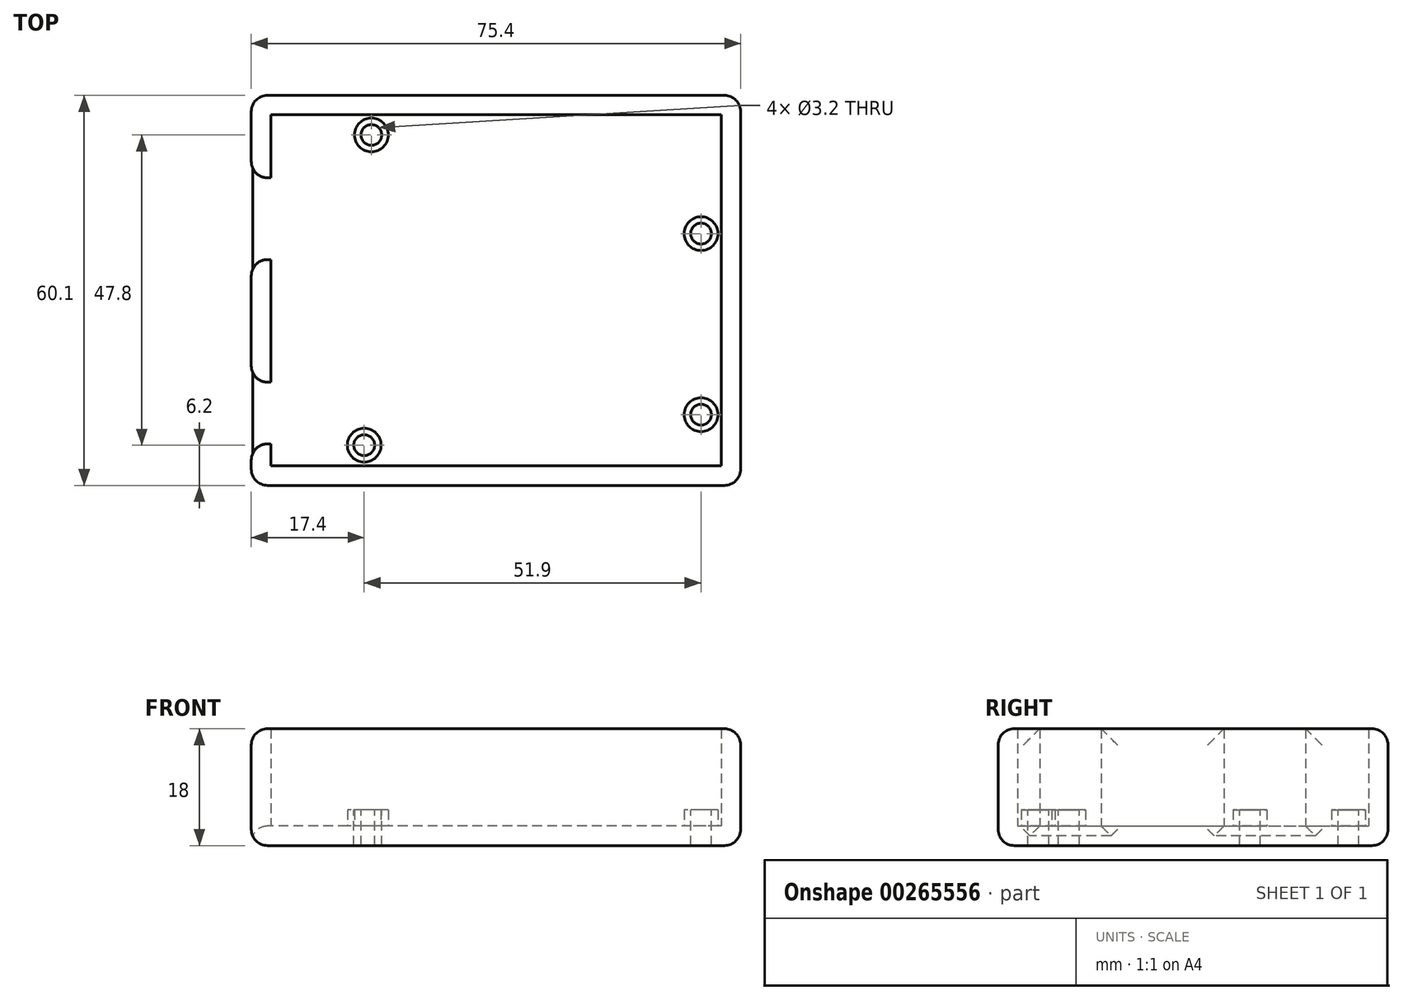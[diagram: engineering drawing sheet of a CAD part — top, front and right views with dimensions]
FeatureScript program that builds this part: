
annotation { "Feature Type Name" : "Feature", "Feature Type Description" : "" }
export const myFeature = defineFeature(function(context is Context, id is Id, definition is map)
    precondition{}
    {
        {
            var Q0;
            Q0=qCreatedBy(makeId("Top.planeOp"),FACE);
            var sketch = newSketch(context, id + "F0", { "sketchPlane" : qUnion([Q0])});
            skLineSegment(sketch, "E0.bottom", {"start": v(34.3, -26.65) * mm, "end": v(-34.3, -26.65) * mm});
            skLineSegment(sketch, "E0.top", {"start": v(34.3, 26.65) * mm, "end": v(-34.3, 26.65) * mm});
            skLineSegment(sketch, "E0.left", {"start": v(34.3, -26.65) * mm, "end": v(34.3, 26.65) * mm});
            skLineSegment(sketch, "E0.right", {"start": v(-34.3, -26.65) * mm, "end": v(-34.3, 26.65) * mm});
            skPoint(sketch, "E0.middle", {"position": v(0, 0) * mm});
            skCircle(sketch, "E1", {"center": v(-19.2, 23.95) * mm, "radius": 1.6 * mm});
            skCircle(sketch, "E2", {"center": v(31.6, 8.75) * mm, "radius": 1.6 * mm});
            skCircle(sketch, "E3", {"center": v(31.6, -19.15) * mm, "radius": 1.6 * mm});
            skCircle(sketch, "E4", {"center": v(-20.3, -23.85) * mm, "radius": 1.6 * mm});
            skLineSegment(sketch, "E5.0", {"start": v(34.7, 27.05) * mm, "end": v(-34.7, 27.05) * mm});
            skLineSegment(sketch, "E5.1", {"start": v(34.7, -27.05) * mm, "end": v(34.7, 27.05) * mm});
            skLineSegment(sketch, "E5.2", {"start": v(34.7, -27.05) * mm, "end": v(-34.7, -27.05) * mm});
            skLineSegment(sketch, "E5.3", {"start": v(-34.7, -27.05) * mm, "end": v(-34.7, 27.05) * mm});
            skLineSegment(sketch, "E6.0", {"start": v(37.7, 30.05) * mm, "end": v(-37.7, 30.05) * mm});
            skLineSegment(sketch, "E6.1", {"start": v(37.7, -30.05) * mm, "end": v(37.7, 30.05) * mm});
            skLineSegment(sketch, "E6.2", {"start": v(37.7, -30.05) * mm, "end": v(-37.7, -30.05) * mm});
            skLineSegment(sketch, "E6.3", {"start": v(-37.7, -30.05) * mm, "end": v(-37.7, 30.05) * mm});
            skLineSegment(sketch, "E7.bottom", {"start": v(-24, 5.05) * mm, "end": v(-40.5, 5.05) * mm});
            skLineSegment(sketch, "E7.top", {"start": v(-24, 17.05) * mm, "end": v(-40.5, 17.05) * mm});
            skLineSegment(sketch, "E7.left", {"start": v(-24, 5.05) * mm, "end": v(-24, 17.05) * mm});
            skLineSegment(sketch, "E7.right", {"start": v(-40.5, 5.05) * mm, "end": v(-40.5, 17.05) * mm});
            skPoint(sketch, "E7.middle", {"position": v(-32.25, 11.05) * mm});
            skLineSegment(sketch, "E8.bottom", {"start": v(-24.8, -23.35) * mm, "end": v(-39.3, -23.35) * mm});
            skLineSegment(sketch, "E8.top", {"start": v(-24.8, -14.45) * mm, "end": v(-39.3, -14.45) * mm});
            skLineSegment(sketch, "E8.left", {"start": v(-24.8, -23.35) * mm, "end": v(-24.8, -14.45) * mm});
            skLineSegment(sketch, "E8.right", {"start": v(-39.3, -23.35) * mm, "end": v(-39.3, -14.45) * mm});
            skPoint(sketch, "E8.middle", {"position": v(-32.05, -18.9) * mm});
            skCircle(sketch, "E9.0", {"center": v(-19.2, 23.95) * mm, "radius": 2.6 * mm});
            skCircle(sketch, "E10.0", {"center": v(-20.3, -23.85) * mm, "radius": 2.6 * mm});
            skCircle(sketch, "E11.0", {"center": v(31.6, -19.15) * mm, "radius": 2.6 * mm});
            skCircle(sketch, "E12.0", {"center": v(31.6, 8.75) * mm, "radius": 2.6 * mm});
            skLineSegment(sketch, "E13.0", {"start": v(-23.7, 4.75) * mm, "end": v(-40.8, 4.75) * mm});
            skLineSegment(sketch, "E13.1", {"start": v(-23.7, 4.75) * mm, "end": v(-23.7, 17.35) * mm});
            skLineSegment(sketch, "E13.2", {"start": v(-23.7, 17.35) * mm, "end": v(-40.8, 17.35) * mm});
            skLineSegment(sketch, "E13.3", {"start": v(-40.8, 4.75) * mm, "end": v(-40.8, 17.35) * mm});
            skLineSegment(sketch, "E14.0", {"start": v(-24.5, -14.15) * mm, "end": v(-39.6, -14.15) * mm});
            skLineSegment(sketch, "E14.1", {"start": v(-24.5, -23.65) * mm, "end": v(-24.5, -14.15) * mm});
            skLineSegment(sketch, "E14.2", {"start": v(-24.5, -23.65) * mm, "end": v(-39.6, -23.65) * mm});
            skLineSegment(sketch, "E14.3", {"start": v(-39.6, -23.65) * mm, "end": v(-39.6, -14.15) * mm});
            skSolve(sketch);
        }
        {
            var Q0;
            {var subQ4=sQuery(id+"F0.wireOp",EDGE,"E5.0");Q0=makeQuery(id+"F0.imprint","IMPRINT",FACE,{"disambiguationData":[TD([[makeQuery(id+"F0.imprint","IMPRINT",EDGE,{"derivedFrom":subQ4}),-1.0]])]});}
            var Q1;
            {var subQ0=sQuery(id+"F0.wireOp",EDGE,"E8.top");var subQ1=sQuery(id+"F0.wireOp",EDGE,"E0.right");var subQ2=makeQuery(id+"F0.imprint","INTERSECT",VERTEX,{"derivedFrom":[subQ1,subQ0]});Q1=makeQuery(id+"F0.imprint","IMPRINT",FACE,{"disambiguationData":[TD([[makeQuery(id+"F0.imprint","IMPRINT",EDGE,{"disambiguationData":[TD([[subQ2,-1.0]])],"derivedFrom":subQ1}),1.0]])]});}
            var Q2;
            {var subQ0=sQuery(id+"F0.wireOp",EDGE,"E8.bottom");var subQ1=sQuery(id+"F0.wireOp",EDGE,"E0.right");var subQ2=makeQuery(id+"F0.imprint","INTERSECT",VERTEX,{"derivedFrom":[subQ1,subQ0]});Q2=makeQuery(id+"F0.imprint","IMPRINT",FACE,{"disambiguationData":[TD([[makeQuery(id+"F0.imprint","IMPRINT",EDGE,{"disambiguationData":[TD([[subQ2,-1.0]])],"derivedFrom":subQ1}),1.0]])]});}
            var Q3;
            {var subQ0=sQuery(id+"F0.wireOp",EDGE,"E8.bottom");var subQ1=sQuery(id+"F0.wireOp",EDGE,"E0.right");var subQ2=makeQuery(id+"F0.imprint","INTERSECT",VERTEX,{"derivedFrom":[subQ1,subQ0]});Q3=makeQuery(id+"F0.imprint","IMPRINT",FACE,{"disambiguationData":[TD([[makeQuery(id+"F0.imprint","IMPRINT",EDGE,{"disambiguationData":[TD([[subQ2,-1.0]])],"derivedFrom":subQ1}),-1.0]])]});}
            var Q4;
            {var subQ4=sQuery(id+"F0.wireOp",EDGE,"E0.bottom");Q4=makeQuery(id+"F0.imprint","IMPRINT",FACE,{"disambiguationData":[TD([[makeQuery(id+"F0.imprint","IMPRINT",EDGE,{"derivedFrom":subQ4}),-1.0]])]});}
            var Q5;
            {var subQ10=sQuery(id+"F0.wireOp",EDGE,"E0.bottom");Q5=makeQuery(id+"F0.imprint","IMPRINT",FACE,{"disambiguationData":[TD([[makeQuery(id+"F0.imprint","IMPRINT",EDGE,{"derivedFrom":subQ10}),1.0]])]});}
            var Q6;
            {var subQ5=sQuery(id+"F0.wireOp",EDGE,"E7.left");Q6=makeQuery(id+"F0.imprint","IMPRINT",FACE,{"disambiguationData":[TD([[makeQuery(id+"F0.imprint","IMPRINT",EDGE,{"derivedFrom":subQ5}),1.0]])]});}
            var Q7;
            {var subQ0=sQuery(id+"F0.wireOp",EDGE,"E7.bottom");var subQ1=sQuery(id+"F0.wireOp",EDGE,"E5.3");var subQ2=makeQuery(id+"F0.imprint","INTERSECT",VERTEX,{"derivedFrom":[subQ1,subQ0]});Q7=makeQuery(id+"F0.imprint","IMPRINT",FACE,{"disambiguationData":[TD([[makeQuery(id+"F0.imprint","IMPRINT",EDGE,{"disambiguationData":[TD([[subQ2,-1.0]])],"derivedFrom":subQ1}),1.0]])]});}
            var Q8;
            {var subQ0=sQuery(id+"F0.wireOp",EDGE,"E7.bottom");var subQ1=sQuery(id+"F0.wireOp",EDGE,"E0.right");var subQ2=makeQuery(id+"F0.imprint","INTERSECT",VERTEX,{"derivedFrom":[subQ1,subQ0]});Q8=makeQuery(id+"F0.imprint","IMPRINT",FACE,{"disambiguationData":[TD([[makeQuery(id+"F0.imprint","IMPRINT",EDGE,{"disambiguationData":[TD([[subQ2,-1.0]])],"derivedFrom":subQ1}),1.0]])]});}
            var Q9;
            {var subQ0=sQuery(id+"F0.wireOp",EDGE,"E8.bottom");var subQ1=sQuery(id+"F0.wireOp",EDGE,"E5.3");var subQ2=makeQuery(id+"F0.imprint","INTERSECT",VERTEX,{"derivedFrom":[subQ1,subQ0]});Q9=makeQuery(id+"F0.imprint","IMPRINT",FACE,{"disambiguationData":[TD([[makeQuery(id+"F0.imprint","IMPRINT",EDGE,{"disambiguationData":[TD([[subQ2,-1.0]])],"derivedFrom":subQ1}),1.0]])]});}
            var Q10;
            {var subQ0=sQuery(id+"F0.wireOp",EDGE,"E8.top");var subQ1=sQuery(id+"F0.wireOp",EDGE,"E5.3");var subQ2=makeQuery(id+"F0.imprint","INTERSECT",VERTEX,{"derivedFrom":[subQ1,subQ0]});Q10=makeQuery(id+"F0.imprint","IMPRINT",FACE,{"disambiguationData":[TD([[makeQuery(id+"F0.imprint","IMPRINT",EDGE,{"disambiguationData":[TD([[subQ2,-1.0]])],"derivedFrom":subQ1}),1.0]])]});}
            var Q11;
            Q11=makeQuery(id+"F0.imprint","IMPRINT",FACE,{"disambiguationData":[TD([[makeQuery(id+"F0.imprint","IMPRINT",EDGE,{"derivedFrom":sQuery(id+"F0.wireOp",EDGE,"E1")}),-1.0]])]});
            var Q12;
            Q12=makeQuery(id+"F0.imprint","IMPRINT",FACE,{"disambiguationData":[TD([[makeQuery(id+"F0.imprint","IMPRINT",EDGE,{"derivedFrom":sQuery(id+"F0.wireOp",EDGE,"E4")}),-1.0]])]});
            var Q13;
            Q13=makeQuery(id+"F0.imprint","IMPRINT",FACE,{"disambiguationData":[TD([[makeQuery(id+"F0.imprint","IMPRINT",EDGE,{"derivedFrom":sQuery(id+"F0.wireOp",EDGE,"E3")}),-1.0]])]});
            var Q14;
            Q14=makeQuery(id+"F0.imprint","IMPRINT",FACE,{"disambiguationData":[TD([[makeQuery(id+"F0.imprint","IMPRINT",EDGE,{"derivedFrom":sQuery(id+"F0.wireOp",EDGE,"E2")}),-1.0]])]});
            var Q15;
            {var subQ0=sQuery(id+"F0.wireOp",EDGE,"E13.0");var subQ1=sQuery(id+"F0.wireOp",EDGE,"E5.3");var subQ2=makeQuery(id+"F0.imprint","INTERSECT",VERTEX,{"derivedFrom":[subQ1,subQ0]});Q15=makeQuery(id+"F0.imprint","IMPRINT",FACE,{"disambiguationData":[TD([[makeQuery(id+"F0.imprint","IMPRINT",EDGE,{"disambiguationData":[TD([[subQ2,-1.0]])],"derivedFrom":subQ1}),1.0]])]});}
            var Q16;
            {var subQ0=sQuery(id+"F0.wireOp",EDGE,"E13.0");var subQ1=sQuery(id+"F0.wireOp",EDGE,"E0.right");var subQ2=makeQuery(id+"F0.imprint","INTERSECT",VERTEX,{"derivedFrom":[subQ1,subQ0]});Q16=makeQuery(id+"F0.imprint","IMPRINT",FACE,{"disambiguationData":[TD([[makeQuery(id+"F0.imprint","IMPRINT",EDGE,{"disambiguationData":[TD([[subQ2,-1.0]])],"derivedFrom":subQ1}),1.0]])]});}
            var Q17;
            {var subQ0=sQuery(id+"F0.wireOp",EDGE,"E7.left");Q17=makeQuery(id+"F0.imprint","IMPRINT",FACE,{"disambiguationData":[TD([[makeQuery(id+"F0.imprint","IMPRINT",EDGE,{"derivedFrom":subQ0}),-1.0]])]});}
            var Q18;
            {var subQ0=sQuery(id+"F0.wireOp",EDGE,"E14.0");var subQ1=sQuery(id+"F0.wireOp",EDGE,"E0.right");var subQ2=makeQuery(id+"F0.imprint","INTERSECT",VERTEX,{"derivedFrom":[subQ1,subQ0]});Q18=makeQuery(id+"F0.imprint","IMPRINT",FACE,{"disambiguationData":[TD([[makeQuery(id+"F0.imprint","IMPRINT",EDGE,{"disambiguationData":[TD([[subQ2,-1.0]])],"derivedFrom":subQ1}),1.0]])]});}
            var Q19;
            {var subQ0=sQuery(id+"F0.wireOp",EDGE,"E14.0");var subQ1=sQuery(id+"F0.wireOp",EDGE,"E5.3");var subQ2=makeQuery(id+"F0.imprint","INTERSECT",VERTEX,{"derivedFrom":[subQ1,subQ0]});Q19=makeQuery(id+"F0.imprint","IMPRINT",FACE,{"disambiguationData":[TD([[makeQuery(id+"F0.imprint","IMPRINT",EDGE,{"disambiguationData":[TD([[subQ2,-1.0]])],"derivedFrom":subQ1}),1.0]])]});}
            var Q20;
            {var subQ0=sQuery(id+"F0.wireOp",EDGE,"E8.left");Q20=makeQuery(id+"F0.imprint","IMPRINT",FACE,{"disambiguationData":[TD([[makeQuery(id+"F0.imprint","IMPRINT",EDGE,{"derivedFrom":subQ0}),-1.0]])]});}
            var Q21;
            {var subQ0=sQuery(id+"F0.wireOp",EDGE,"E7.top");var subQ1=sQuery(id+"F0.wireOp",EDGE,"E5.3");var subQ2=makeQuery(id+"F0.imprint","INTERSECT",VERTEX,{"derivedFrom":[subQ1,subQ0]});Q21=makeQuery(id+"F0.imprint","IMPRINT",FACE,{"disambiguationData":[TD([[makeQuery(id+"F0.imprint","IMPRINT",EDGE,{"disambiguationData":[TD([[subQ2,-1.0]])],"derivedFrom":subQ1}),1.0]])]});}
            var Q22;
            {var subQ0=sQuery(id+"F0.wireOp",EDGE,"E7.top");var subQ1=sQuery(id+"F0.wireOp",EDGE,"E0.right");var subQ2=makeQuery(id+"F0.imprint","INTERSECT",VERTEX,{"derivedFrom":[subQ1,subQ0]});Q22=makeQuery(id+"F0.imprint","IMPRINT",FACE,{"disambiguationData":[TD([[makeQuery(id+"F0.imprint","IMPRINT",EDGE,{"disambiguationData":[TD([[subQ2,-1.0]])],"derivedFrom":subQ1}),1.0]])]});}
            var Q23;
            {var subQ0=sQuery(id+"F0.wireOp",EDGE,"E14.2");var subQ1=sQuery(id+"F0.wireOp",EDGE,"E0.right");var subQ2=makeQuery(id+"F0.imprint","INTERSECT",VERTEX,{"derivedFrom":[subQ1,subQ0]});Q23=makeQuery(id+"F0.imprint","IMPRINT",FACE,{"disambiguationData":[TD([[makeQuery(id+"F0.imprint","IMPRINT",EDGE,{"disambiguationData":[TD([[subQ2,-1.0]])],"derivedFrom":subQ1}),1.0]])]});}
            var Q24;
            {var subQ0=sQuery(id+"F0.wireOp",EDGE,"E14.2");var subQ1=sQuery(id+"F0.wireOp",EDGE,"E5.3");var subQ2=makeQuery(id+"F0.imprint","INTERSECT",VERTEX,{"derivedFrom":[subQ1,subQ0]});Q24=makeQuery(id+"F0.imprint","IMPRINT",FACE,{"disambiguationData":[TD([[makeQuery(id+"F0.imprint","IMPRINT",EDGE,{"disambiguationData":[TD([[subQ2,-1.0]])],"derivedFrom":subQ1}),1.0]])]});}
            extrude(context, id + "F1", {"entities" : qUnion([Q0, Q1, Q2, Q3, Q4, Q5, Q6, Q7, Q8, Q9, Q10, Q11, Q12, Q13, Q14, Q15, Q16, Q17, Q18, Q19, Q20, Q21, Q22, Q23, Q24]), "oppositeDirection" : true, "depth" : 3 * mm});
        }
        {
            var Q0;
            {var subQ11=sQuery(id+"F0.wireOp",EDGE,"E5.0");Q0=makeQuery(id+"F0.imprint","IMPRINT",FACE,{"disambiguationData":[TD([[makeQuery(id+"F0.imprint","IMPRINT",EDGE,{"derivedFrom":subQ11}),-1.0]])]});}
            var Q1;
            {var subQ0=sQuery(id+"F0.wireOp",EDGE,"E14.0");var subQ1=sQuery(id+"F0.wireOp",EDGE,"E5.3");var subQ2=makeQuery(id+"F0.imprint","INTERSECT",VERTEX,{"derivedFrom":[subQ1,subQ0]});Q1=makeQuery(id+"F0.imprint","IMPRINT",FACE,{"disambiguationData":[TD([[makeQuery(id+"F0.imprint","IMPRINT",EDGE,{"disambiguationData":[TD([[subQ2,-1.0]])],"derivedFrom":subQ1}),1.0]])]});}
            extrude(context, id + "F2", {"entities" : qUnion([Q0, Q1]), "operationType" : NewBodyOperationType.ADD, "depth" : 15 * mm});
        }
        {
            var Q0;
            Q0=makeQuery(id+"F0.imprint","IMPRINT",FACE,{"disambiguationData":[TD([[makeQuery(id+"F0.imprint","IMPRINT",EDGE,{"derivedFrom":sQuery(id+"F0.wireOp",EDGE,"E4")}),-1.0]])]});
            var Q1;
            Q1=makeQuery(id+"F0.imprint","IMPRINT",FACE,{"disambiguationData":[TD([[makeQuery(id+"F0.imprint","IMPRINT",EDGE,{"derivedFrom":sQuery(id+"F0.wireOp",EDGE,"E1")}),-1.0]])]});
            var Q2;
            Q2=makeQuery(id+"F0.imprint","IMPRINT",FACE,{"disambiguationData":[TD([[makeQuery(id+"F0.imprint","IMPRINT",EDGE,{"derivedFrom":sQuery(id+"F0.wireOp",EDGE,"E2")}),-1.0]])]});
            var Q3;
            Q3=makeQuery(id+"F0.imprint","IMPRINT",FACE,{"disambiguationData":[TD([[makeQuery(id+"F0.imprint","IMPRINT",EDGE,{"derivedFrom":sQuery(id+"F0.wireOp",EDGE,"E3")}),-1.0]])]});
            extrude(context, id + "F3", {"entities" : qUnion([Q0, Q1, Q2, Q3]), "operationType" : NewBodyOperationType.ADD, "depth" : 2.5 * mm});
        }
        {
            var Q0;
            {var subQ0=sQuery(id+"F0.wireOp",EDGE,"E6.2");var subQ1=sQuery(id+"F0.wireOp",EDGE,"E6.1");Q0=makeQuery(id+"F2.boolean.opBoolean","MERGE",EDGE,{"derivedFrom":[makeQuery(id+"F1.opExtrude","SWEPT_EDGE",EDGE,{"disambiguationData":[OSD([subQ1,subQ0])]}),makeQuery(id+"F2.opExtrude","SWEPT_EDGE",EDGE,{"disambiguationData":[OSD([subQ1,subQ0])]})]});}
            var Q1;
            {var subQ0=sQuery(id+"F0.wireOp",EDGE,"E6.1");var subQ1=sQuery(id+"F0.wireOp",EDGE,"E6.0");Q1=makeQuery(id+"F2.boolean.opBoolean","MERGE",EDGE,{"derivedFrom":[makeQuery(id+"F1.opExtrude","SWEPT_EDGE",EDGE,{"disambiguationData":[OSD([subQ1,subQ0])]}),makeQuery(id+"F2.opExtrude","SWEPT_EDGE",EDGE,{"disambiguationData":[OSD([subQ1,subQ0])]})]});}
            var Q2;
            {var subQ0=sQuery(id+"F0.wireOp",EDGE,"E6.3");var subQ1=sQuery(id+"F0.wireOp",EDGE,"E6.0");Q2=makeQuery(id+"F2.boolean.opBoolean","MERGE",EDGE,{"derivedFrom":[makeQuery(id+"F1.opExtrude","SWEPT_EDGE",EDGE,{"disambiguationData":[OSD([subQ1,subQ0])]}),makeQuery(id+"F2.opExtrude","SWEPT_EDGE",EDGE,{"disambiguationData":[OSD([subQ1,subQ0])]})]});}
            var Q3;
            {var subQ0=sQuery(id+"F0.wireOp",EDGE,"E6.3");var subQ1=sQuery(id+"F0.wireOp",EDGE,"E6.2");Q3=makeQuery(id+"F2.boolean.opBoolean","MERGE",EDGE,{"derivedFrom":[makeQuery(id+"F1.opExtrude","SWEPT_EDGE",EDGE,{"disambiguationData":[OSD([subQ1,subQ0])]}),makeQuery(id+"F2.opExtrude","SWEPT_EDGE",EDGE,{"disambiguationData":[OSD([subQ1,subQ0])]})]});}
            var Q4;
            Q4=makeQuery(id+"F2.opExtrude","SWEPT_EDGE",EDGE,{"disambiguationData":[OSD([sQuery(id+"F0.wireOp",EDGE,"E6.3"),sQuery(id+"F0.wireOp",EDGE,"E14.0")])]});
            var Q5;
            Q5=makeQuery(id+"F2.opExtrude","SWEPT_EDGE",EDGE,{"disambiguationData":[OSD([sQuery(id+"F0.wireOp",EDGE,"E6.3"),sQuery(id+"F0.wireOp",EDGE,"E13.2")])]});
            var Q6;
            Q6=makeQuery(id+"F2.opExtrude","SWEPT_EDGE",EDGE,{"disambiguationData":[OSD([sQuery(id+"F0.wireOp",EDGE,"E6.3"),sQuery(id+"F0.wireOp",EDGE,"E13.0")])]});
            var Q7;
            Q7=makeQuery(id+"F2.opExtrude","SWEPT_EDGE",EDGE,{"disambiguationData":[OSD([sQuery(id+"F0.wireOp",EDGE,"E6.3"),sQuery(id+"F0.wireOp",EDGE,"E14.2")])]});
            var Q8;
            {var subQ0=sQuery(id+"F0.wireOp",EDGE,"E5.3");Q8=makeQuery(id+"F2.opExtrude","CAP_EDGE",EDGE,{"disambiguationData":[OSD([subQ0]),TDD([makeQuery(id+"F0.imprint","IMPRINT",EDGE,{"disambiguationData":[TD([[makeQuery(id+"F0.imprint","INTERSECT",VERTEX,{"derivedFrom":[sQuery(id+"F0.wireOp",EDGE,"E5.0"),subQ0]}),1.0]])],"derivedFrom":subQ0})])],"isStart":true});}
            var Q9;
            Q9=makeQuery(id+"F2.opExtrude","CAP_EDGE",EDGE,{"disambiguationData":[OSD([sQuery(id+"F0.wireOp",EDGE,"E5.0")])],"isStart":true});
            var Q10;
            {var subQ0=sQuery(id+"F0.wireOp",EDGE,"E5.3");Q10=makeQuery(id+"F2.opExtrude","CAP_EDGE",EDGE,{"disambiguationData":[OSD([subQ0]),TDD([makeQuery(id+"F0.imprint","IMPRINT",EDGE,{"disambiguationData":[TD([[makeQuery(id+"F0.imprint","INTERSECT",VERTEX,{"derivedFrom":[subQ0,sQuery(id+"F0.wireOp",EDGE,"E14.0")]}),-1.0]])],"derivedFrom":subQ0})])],"isStart":true});}
            var Q11;
            {var subQ0=sQuery(id+"F0.wireOp",EDGE,"E5.3");Q11=makeQuery(id+"F2.opExtrude","CAP_EDGE",EDGE,{"disambiguationData":[OSD([subQ0]),TDD([makeQuery(id+"F0.imprint","IMPRINT",EDGE,{"disambiguationData":[TD([[makeQuery(id+"F0.imprint","INTERSECT",VERTEX,{"derivedFrom":[sQuery(id+"F0.wireOp",EDGE,"E5.2"),subQ0]}),-1.0]])],"derivedFrom":subQ0})])],"isStart":true});}
            var Q12;
            Q12=makeQuery(id+"F2.opExtrude","CAP_EDGE",EDGE,{"disambiguationData":[OSD([sQuery(id+"F0.wireOp",EDGE,"E5.2")])],"isStart":true});
            var Q13;
            Q13=makeQuery(id+"F2.opExtrude","CAP_EDGE",EDGE,{"disambiguationData":[OSD([sQuery(id+"F0.wireOp",EDGE,"E5.1")])],"isStart":true});
            var Q14;
            Q14=makeQuery(id+"F3.opExtrude","CAP_EDGE",EDGE,{"disambiguationData":[OSD([sQuery(id+"F0.wireOp",EDGE,"E12.0")])],"isStart":true});
            var Q15;
            Q15=makeQuery(id+"F3.opExtrude","CAP_EDGE",EDGE,{"disambiguationData":[OSD([sQuery(id+"F0.wireOp",EDGE,"E11.0")])],"isStart":true});
            var Q16;
            Q16=makeQuery(id+"F3.opExtrude","CAP_EDGE",EDGE,{"disambiguationData":[OSD([sQuery(id+"F0.wireOp",EDGE,"E10.0")])],"isStart":true});
            var Q17;
            Q17=makeQuery(id+"F3.opExtrude","CAP_EDGE",EDGE,{"disambiguationData":[OSD([sQuery(id+"F0.wireOp",EDGE,"E9.0")])],"isStart":true});
            var Q18;
            {var subQ0=sQuery(id+"F0.wireOp",EDGE,"E6.3");var subQ1=sQuery(id+"F0.wireOp",EDGE,"E13.0");Q18=makeQuery(id+"F2.boolean.opBoolean","SPLIT",EDGE,{"disambiguationData":[TD([makeQuery(id+"F2.opExtrude","SWEPT_FACE",FACE,{"disambiguationData":[OSD([subQ1])]})])],"derivedFrom":makeQuery(id+"F1.opExtrude","CAP_EDGE",EDGE,{"disambiguationData":[OSD([subQ0])],"isStart":true})});}
            var Q19;
            {var subQ0=sQuery(id+"F0.wireOp",EDGE,"E14.0");var subQ1=sQuery(id+"F0.wireOp",EDGE,"E6.3");Q19=makeQuery(id+"F2.boolean.opBoolean","SPLIT",EDGE,{"disambiguationData":[TD([makeQuery(id+"F2.opExtrude","SWEPT_FACE",FACE,{"disambiguationData":[OSD([subQ0])]})])],"derivedFrom":makeQuery(id+"F1.opExtrude","CAP_EDGE",EDGE,{"disambiguationData":[OSD([subQ1])],"isStart":true})});}
            var Q20;
            Q20=makeQuery(id+"F1.opExtrude","CAP_EDGE",EDGE,{"disambiguationData":[OSD([sQuery(id+"F0.wireOp",EDGE,"E6.1")])],"isStart":false});
            var Q21;
            Q21=makeQuery(id+"F1.opExtrude","CAP_EDGE",EDGE,{"disambiguationData":[OSD([sQuery(id+"F0.wireOp",EDGE,"E6.0")])],"isStart":false});
            var Q22;
            Q22=makeQuery(id+"F1.opExtrude","CAP_EDGE",EDGE,{"disambiguationData":[OSD([sQuery(id+"F0.wireOp",EDGE,"E6.3")])],"isStart":false});
            var Q23;
            Q23=makeQuery(id+"F1.opExtrude","CAP_EDGE",EDGE,{"disambiguationData":[OSD([sQuery(id+"F0.wireOp",EDGE,"E6.2")])],"isStart":false});
            var Q24;
            Q24=makeQuery(id+"F2.opExtrude","CAP_EDGE",EDGE,{"disambiguationData":[OSD([sQuery(id+"F0.wireOp",EDGE,"E6.0")])],"isStart":false});
            var Q25;
            Q25=makeQuery(id+"F2.opExtrude","CAP_EDGE",EDGE,{"disambiguationData":[OSD([sQuery(id+"F0.wireOp",EDGE,"E6.2")])],"isStart":false});
            var Q26;
            Q26=makeQuery(id+"F2.opExtrude","CAP_EDGE",EDGE,{"disambiguationData":[OSD([sQuery(id+"F0.wireOp",EDGE,"E6.1")])],"isStart":false});
            var Q27;
            {var subQ0=sQuery(id+"F0.wireOp",EDGE,"E6.3");Q27=makeQuery(id+"F2.opExtrude","CAP_EDGE",EDGE,{"disambiguationData":[OSD([subQ0]),TDD([makeQuery(id+"F0.imprint","IMPRINT",EDGE,{"disambiguationData":[TD([[makeQuery(id+"F0.imprint","INTERSECT",VERTEX,{"derivedFrom":[subQ0,sQuery(id+"F0.wireOp",EDGE,"E14.0")]}),-1.0]])],"derivedFrom":subQ0})])],"isStart":false});}
            var Q28;
            {var subQ0=sQuery(id+"F0.wireOp",EDGE,"E6.3");Q28=makeQuery(id+"F2.opExtrude","CAP_EDGE",EDGE,{"disambiguationData":[OSD([subQ0]),TDD([makeQuery(id+"F0.imprint","IMPRINT",EDGE,{"disambiguationData":[TD([[makeQuery(id+"F0.imprint","INTERSECT",VERTEX,{"derivedFrom":[sQuery(id+"F0.wireOp",EDGE,"E6.0"),subQ0]}),1.0]])],"derivedFrom":subQ0})])],"isStart":false});}
            var Q29;
            {var subQ0=sQuery(id+"F0.wireOp",EDGE,"E6.3");Q29=makeQuery(id+"F2.opExtrude","CAP_EDGE",EDGE,{"disambiguationData":[OSD([subQ0]),TDD([makeQuery(id+"F0.imprint","IMPRINT",EDGE,{"disambiguationData":[TD([[makeQuery(id+"F0.imprint","INTERSECT",VERTEX,{"derivedFrom":[sQuery(id+"F0.wireOp",EDGE,"E6.2"),subQ0]}),-1.0]])],"derivedFrom":subQ0})])],"isStart":false});}
            fillet(context, id + "F4", {"entities" : qUnion([Q0, Q1, Q2, Q3, Q4, Q5, Q6, Q7, Q8, Q9, Q10, Q11, Q12, Q13, Q14, Q15, Q16, Q17, Q18, Q19, Q20, Q21, Q22, Q23, Q24, Q25, Q26, Q27, Q28, Q29]), "radius" : 2.5 * mm, "tangentPropagation" : true, "allowEdgeOverflow" : false});
        }
    });
